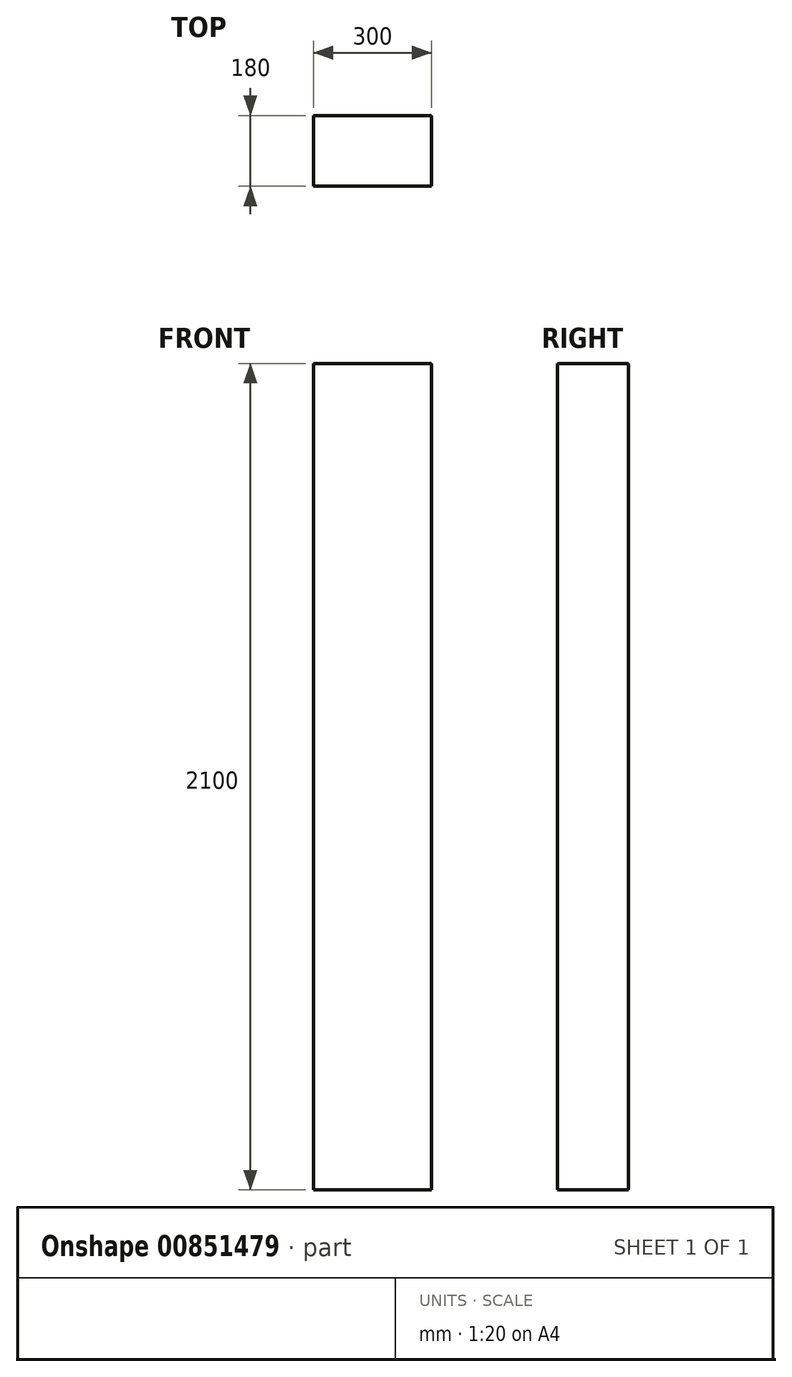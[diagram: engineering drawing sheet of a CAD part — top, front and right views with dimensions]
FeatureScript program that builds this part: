
annotation { "Feature Type Name" : "Feature", "Feature Type Description" : "" }
export const myFeature = defineFeature(function(context is Context, id is Id, definition is map)
    precondition{}
    {
        {
            var Q0;
            Q0=qCreatedBy(makeId("Front.planeOp"),FACE);
            var sketch = newSketch(context, id + "F0", { "sketchPlane" : qUnion([Q0])});
            skLineSegment(sketch, "E0.bottom", {"start": v(-272.84, 1993.85) * mm, "end": v(27.16, 1993.85) * mm});
            skLineSegment(sketch, "E0.top", {"start": v(-272.84, -106.15) * mm, "end": v(27.16, -106.15) * mm});
            skLineSegment(sketch, "E0.left", {"start": v(-272.84, 1993.85) * mm, "end": v(-272.84, -106.15) * mm});
            skLineSegment(sketch, "E0.right", {"start": v(27.16, 1993.85) * mm, "end": v(27.16, -106.15) * mm});
            skSolve(sketch);
        }
        {
            var Q0;
            Q0 = qSketchRegion(id + "F0", true);
            extrude(context, id + "F1", {"entities" : qUnion([Q0]), "depth" : 180 * mm, "offsetDistance" : 25 * mm});
        }
    });
